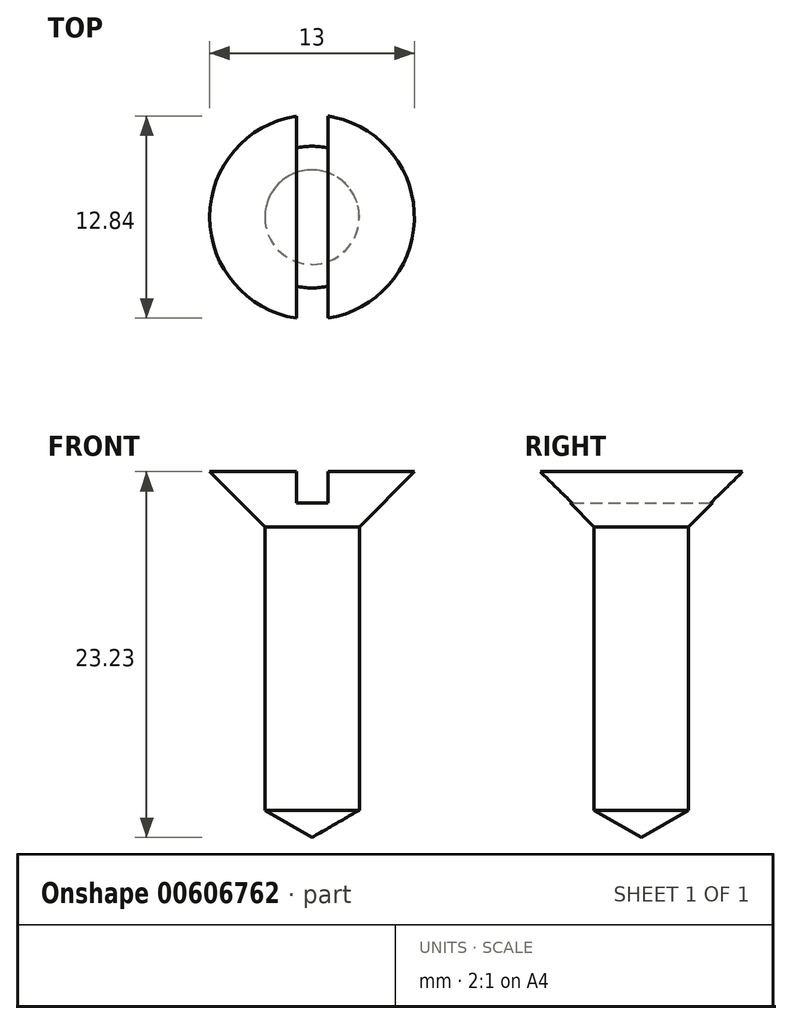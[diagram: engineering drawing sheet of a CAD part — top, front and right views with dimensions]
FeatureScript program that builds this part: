
annotation { "Feature Type Name" : "Feature", "Feature Type Description" : "" }
export const myFeature = defineFeature(function(context is Context, id is Id, definition is map)
    precondition{}
    {
        {
            var Q0;
            Q0=qCreatedBy(makeId("Front.planeOp"),FACE);
            var sketch = newSketch(context, id + "F0", { "sketchPlane" : qUnion([Q0])});
            skLineSegment(sketch, "E0", {"start": v(0, 0) * mm, "end": v(3, 1.73) * mm});
            skLineSegment(sketch, "E1", {"start": v(3, 1.73) * mm, "end": v(3, 19.73) * mm});
            skLineSegment(sketch, "E2", {"start": v(3, 19.73) * mm, "end": v(6.5, 23.23) * mm});
            skLineSegment(sketch, "E3", {"start": v(6.5, 23.23) * mm, "end": v(0, 23.23) * mm});
            skLineSegment(sketch, "E4", {"start": v(0, 23.23) * mm, "end": v(0, 0) * mm});
            skSolve(sketch);
        }
        {
            var Q0;
            Q0=qCreatedBy(makeId("Front.planeOp"),FACE);
            var sketch = newSketch(context, id + "F1", { "sketchPlane" : qUnion([Q0])});
            skLineSegment(sketch, "E5", {"start": v(0, 0) * mm, "end": v(0, 44.8) * mm});
            skSolve(sketch);
        }
        {
            var Q0;
            Q0=makeQuery(id+"F0.imprint","IMPRINT",FACE,{"disambiguationData":[TD([[makeQuery(id+"F0.imprint","IMPRINT",EDGE,{"derivedFrom":sQuery(id+"F0.wireOp",EDGE,"E0")}),1.0]])]});
            var Q1;
            Q1=sQuery(id+"F1.wireOp",EDGE,"E5");
            revolve(context, id + "F2", {"entities" : qUnion([Q0]), "axis" : qUnion([Q1]), "revolveType" : RevolveType.FULL});
        }
        {
            var Q0;
            Q0=qCreatedBy(makeId("Front.planeOp"),FACE);
            var sketch = newSketch(context, id + "F3", { "sketchPlane" : qUnion([Q0])});
            skLineSegment(sketch, "E6.bottom", {"start": v(1, 21.23) * mm, "end": v(-1, 21.23) * mm});
            skLineSegment(sketch, "E6.top", {"start": v(1, 26.38) * mm, "end": v(-1, 26.38) * mm});
            skLineSegment(sketch, "E6.left", {"start": v(1, 21.23) * mm, "end": v(1, 26.38) * mm});
            skLineSegment(sketch, "E6.right", {"start": v(-1, 21.23) * mm, "end": v(-1, 26.38) * mm});
            skPoint(sketch, "E6.middle", {"position": v(0, 23.8) * mm});
            skSolve(sketch);
        }
        {
            var Q0;
            Q0=makeQuery(id+"F3.imprint","IMPRINT",FACE,{"disambiguationData":[TD([[makeQuery(id+"F3.imprint","IMPRINT",EDGE,{"derivedFrom":sQuery(id+"F3.wireOp",EDGE,"E6.bottom")}),-1.0]])]});
            extrude(context, id + "F4", {"entities" : qUnion([Q0]), "operationType" : NewBodyOperationType.REMOVE, "endBound" : BoundingType.SYMMETRIC, "depth" : 25 * mm, "offsetDistance" : 25 * mm});
        }
    });
